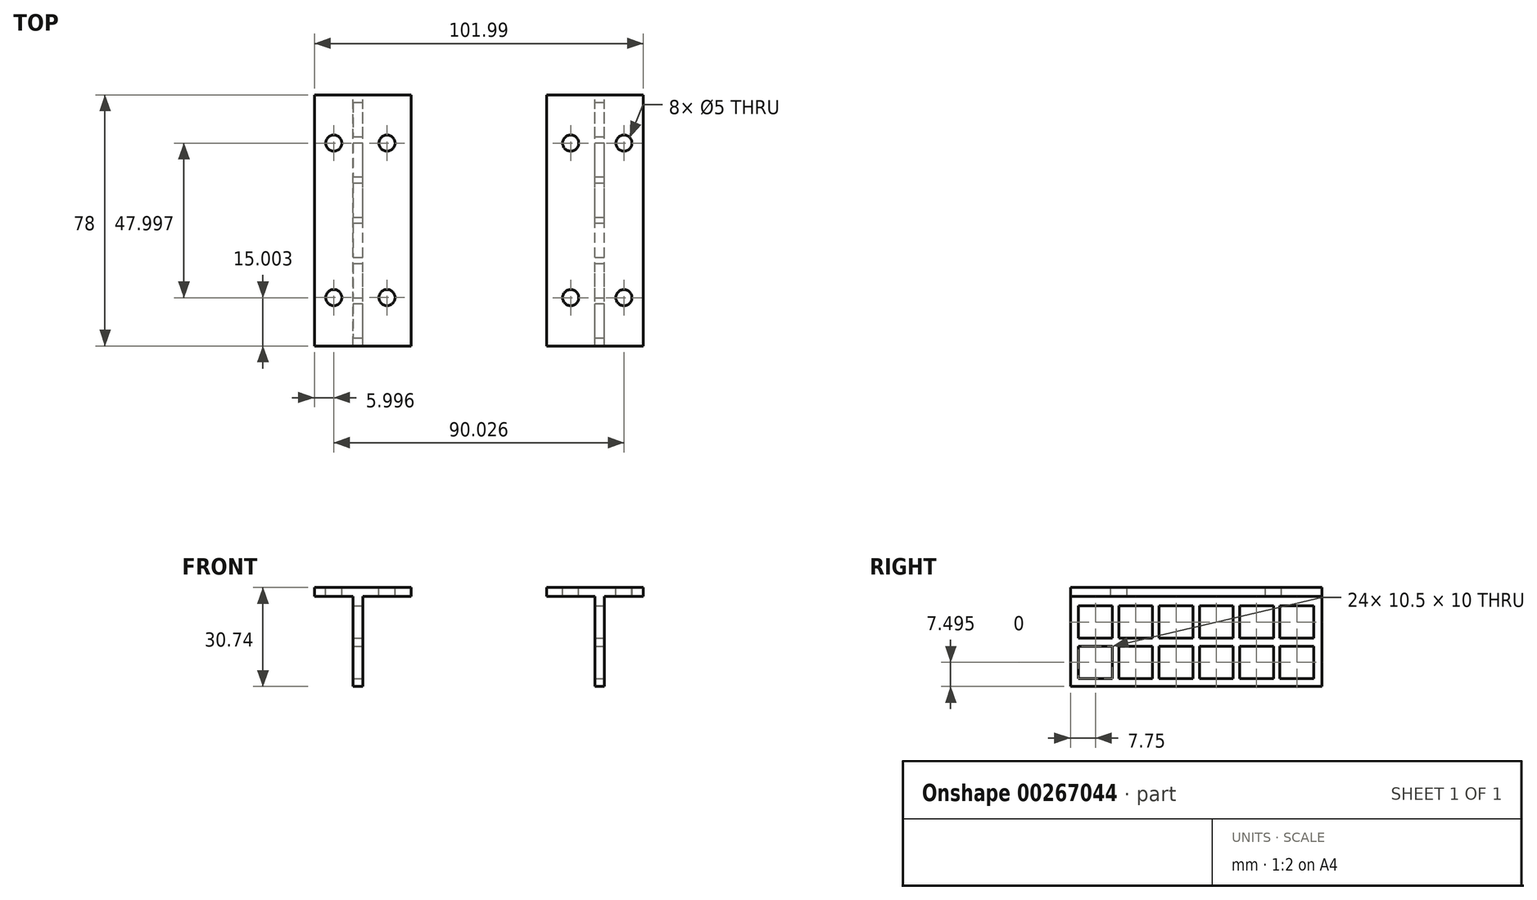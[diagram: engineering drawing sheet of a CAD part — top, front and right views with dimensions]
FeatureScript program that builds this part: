
annotation { "Feature Type Name" : "Feature", "Feature Type Description" : "" }
export const myFeature = defineFeature(function(context is Context, id is Id, definition is map)
    precondition{}
    {
        {
            var Q0;
            Q0=qCreatedBy(makeId("Front.planeOp"),FACE);
            var sketch = newSketch(context, id + "F0", { "sketchPlane" : qUnion([Q0])});
            skLineSegment(sketch, "E0", {"start": v(36.03, -9.62) * mm, "end": v(36.03, 18.38) * mm});
            skLineSegment(sketch, "E1", {"start": v(36.03, 18.38) * mm, "end": v(48.02, 18.38) * mm});
            skLineSegment(sketch, "E2", {"start": v(48.02, 18.38) * mm, "end": v(48.02, 21.12) * mm});
            skLineSegment(sketch, "E3", {"start": v(48.02, 21.12) * mm, "end": v(33.02, 21.12) * mm});
            skLineSegment(sketch, "E4", {"start": v(33.02, 18.38) * mm, "end": v(33.02, -9.62) * mm});
            skLineSegment(sketch, "E5.MirrorCS", {"start": v(-53.97, 18.38) * mm, "end": v(-53.97, 21.12) * mm});
            skLineSegment(sketch, "E6.MirrorCS", {"start": v(-41.97, -9.62) * mm, "end": v(-41.97, 18.38) * mm});
            skLineSegment(sketch, "E7.MirrorCS", {"start": v(-41.97, 18.38) * mm, "end": v(-53.97, 18.38) * mm});
            skLineSegment(sketch, "E8.MirrorCS", {"start": v(-53.97, 21.12) * mm, "end": v(-38.97, 21.12) * mm});
            skLineSegment(sketch, "E9.MirrorCS", {"start": v(-38.97, 18.38) * mm, "end": v(-38.97, -9.62) * mm});
            skPoint(sketch, "E10.MirrorCS.start.orphan", {"position": v(36.03, 18.38) * mm});
            skLineSegment(sketch, "E11", {"start": v(-41.97, -9.62) * mm, "end": v(-38.97, -9.62) * mm});
            skLineSegment(sketch, "E12", {"start": v(36.03, -9.62) * mm, "end": v(33.02, -9.62) * mm});
            skLineSegment(sketch, "E13.MirrorCS", {"start": v(-38.97, 18.38) * mm, "end": v(-23.97, 18.38) * mm});
            skLineSegment(sketch, "E14.MirrorCS", {"start": v(-23.97, 18.38) * mm, "end": v(-23.97, 21.12) * mm});
            skLineSegment(sketch, "E15.MirrorCS", {"start": v(-23.97, 21.12) * mm, "end": v(-38.97, 21.12) * mm});
            skPoint(sketch, "E16.orphan", {"position": v(-35.97, 18.38) * mm});
            skLineSegment(sketch, "E17.MirrorCS", {"start": v(33.02, 18.38) * mm, "end": v(18.02, 18.38) * mm});
            skLineSegment(sketch, "E18.MirrorCS", {"start": v(18.02, 18.38) * mm, "end": v(18.02, 21.12) * mm});
            skLineSegment(sketch, "E19.MirrorCS", {"start": v(18.02, 21.12) * mm, "end": v(33.02, 21.12) * mm});
            skPoint(sketch, "E20.orphan", {"position": v(30.02, 18.38) * mm});
            skSolve(sketch);
        }
        {
            var Q0;
            Q0=qSketchRegion(id+"F0",true);
            extrude(context, id + "F1", {"entities" : qUnion([Q0]), "endBound" : BoundingType.SYMMETRIC, "depth" : 78 * mm});
        }
        {
            var Q0;
            Q0=makeQuery(id+"F1.opExtrude","SWEPT_FACE",FACE,{"disambiguationData":[OSD([sQuery(id+"F0.wireOp",EDGE,"E3")])]});
            var sketch = newSketch(context, id + "F2", { "sketchPlane" : qUnion([Q0])});
            skLineSegment(sketch, "E21", {"start": v(42.02, -39) * mm, "end": v(42.06, 39) * mm, "construction": true});
            skLineSegment(sketch, "E22.0.0", {"start": v(-53.97, 39) * mm, "end": v(-53.97, 39) * mm});
            skLineSegment(sketch, "E22.0.1", {"start": v(-53.97, 39) * mm, "end": v(-53.97, -39) * mm, "construction": true});
            skLineSegment(sketch, "E22.0.2", {"start": v(-53.97, -39) * mm, "end": v(-53.97, -39) * mm});
            skLineSegment(sketch, "E22.0.3", {"start": v(-53.97, -39) * mm, "end": v(-53.97, 39) * mm, "construction": true});
            skLineSegment(sketch, "E23", {"start": v(-47.97, 39) * mm, "end": v(-47.97, -39) * mm, "construction": true});
            skLineSegment(sketch, "E24", {"start": v(-53.97, -23.96) * mm, "end": v(48.02, -24) * mm, "construction": true});
            skLineSegment(sketch, "E25", {"start": v(48.02, 24) * mm, "end": v(-53.97, 24) * mm, "construction": true});
            skLineSegment(sketch, "E26", {"start": v(48.02, -24) * mm, "end": v(48.02, -39) * mm, "construction": true});
            skLineSegment(sketch, "E27", {"start": v(48.02, 39) * mm, "end": v(48.02, 24) * mm, "construction": true});
            skCircle(sketch, "E28", {"center": v(42.03, -24) * mm, "radius": 2.5 * mm});
            skCircle(sketch, "E29", {"center": v(42.05, 24) * mm, "radius": 2.5 * mm});
            skCircle(sketch, "E30", {"center": v(-47.97, 24) * mm, "radius": 2.5 * mm});
            skCircle(sketch, "E31", {"center": v(-47.97, -23.96) * mm, "radius": 2.5 * mm});
            skCircle(sketch, "E32", {"center": v(25.52, -24) * mm, "radius": 2.5 * mm});
            skCircle(sketch, "E33", {"center": v(25.52, 24) * mm, "radius": 2.5 * mm});
            skCircle(sketch, "E34", {"center": v(-31.47, -23.97) * mm, "radius": 2.5 * mm});
            skCircle(sketch, "E35", {"center": v(-31.47, 24) * mm, "radius": 2.5 * mm});
            skLineSegment(sketch, "E36.0", {"start": v(-38.97, -39) * mm, "end": v(-38.97, 39) * mm, "construction": true});
            skLineSegment(sketch, "E37.0", {"start": v(33.02, -39) * mm, "end": v(33.02, 39) * mm, "construction": true});
            skLineSegment(sketch, "E38.0", {"start": v(-23.97, -39) * mm, "end": v(-23.97, 39) * mm, "construction": true});
            skLineSegment(sketch, "E39.0", {"start": v(18.02, -39) * mm, "end": v(18.02, 39) * mm, "construction": true});
            skLineSegment(sketch, "E40", {"start": v(-38.97, -31.27) * mm, "end": v(-23.97, -31.27) * mm, "construction": true});
            skLineSegment(sketch, "E41", {"start": v(33.02, -32.9) * mm, "end": v(18.02, -32.9) * mm, "construction": true});
            skPoint(sketch, "E42", {"position": v(-31.47, -31.27) * mm});
            skPoint(sketch, "E43", {"position": v(25.52, -32.9) * mm});
            skSolve(sketch);
        }
        {
            var Q0;
            Q0=qSketchRegion(id+"F2",true);
            extrude(context, id + "F3", {"entities" : qUnion([Q0]), "operationType" : NewBodyOperationType.REMOVE, "endBound" : BoundingType.UP_TO_NEXT, "oppositeDirection" : true, "depth" : 25 * mm});
        }
        {
            var Q0;
            Q0=makeQuery(id+"F1.opExtrude","SWEPT_FACE",FACE,{"disambiguationData":[OSD([sQuery(id+"F0.wireOp",EDGE,"E0")])]});
            var sketch = newSketch(context, id + "F4", { "sketchPlane" : qUnion([Q0])});
            skLineSegment(sketch, "E44.bottom", {"start": v(-36.5, -7.12) * mm, "end": v(-26.5, -7.12) * mm});
            skLineSegment(sketch, "E44.top", {"start": v(-36.5, 2.88) * mm, "end": v(-26.5, 2.88) * mm});
            skLineSegment(sketch, "E44.left", {"start": v(-36.5, -7.12) * mm, "end": v(-36.5, 2.88) * mm});
            skLineSegment(sketch, "E44.right", {"start": v(-26.5, -7.12) * mm, "end": v(-26.5, 2.88) * mm});
            skLineSegment(sketch, "E45.0.1.0", {"start": v(-36.5, 5.38) * mm, "end": v(-36.5, 15.38) * mm});
            skLineSegment(sketch, "E45.0.1.1", {"start": v(-26.5, 5.38) * mm, "end": v(-26.5, 15.38) * mm});
            skLineSegment(sketch, "E45.0.1.2", {"start": v(-36.5, 5.38) * mm, "end": v(-26.5, 5.38) * mm});
            skLineSegment(sketch, "E45.0.1.3", {"start": v(-36.5, 15.38) * mm, "end": v(-26.5, 15.38) * mm});
            skLineSegment(sketch, "E45.1.0.0", {"start": v(-24, -7.12) * mm, "end": v(-24, 2.88) * mm});
            skLineSegment(sketch, "E45.1.0.1", {"start": v(-14, -7.12) * mm, "end": v(-14, 2.88) * mm});
            skLineSegment(sketch, "E45.1.0.2", {"start": v(-24, -7.12) * mm, "end": v(-14, -7.12) * mm});
            skLineSegment(sketch, "E45.1.0.3", {"start": v(-24, 2.88) * mm, "end": v(-14, 2.88) * mm});
            skLineSegment(sketch, "E45.1.1.0", {"start": v(-24, 5.38) * mm, "end": v(-24, 15.38) * mm});
            skLineSegment(sketch, "E45.1.1.1", {"start": v(-14, 5.38) * mm, "end": v(-14, 15.38) * mm});
            skLineSegment(sketch, "E45.1.1.2", {"start": v(-24, 5.38) * mm, "end": v(-14, 5.38) * mm});
            skLineSegment(sketch, "E45.1.1.3", {"start": v(-24, 15.38) * mm, "end": v(-14, 15.38) * mm});
            skLineSegment(sketch, "E45.2.0.0", {"start": v(-11.5, -7.12) * mm, "end": v(-11.5, 2.88) * mm});
            skLineSegment(sketch, "E45.2.0.1", {"start": v(-1.5, -7.12) * mm, "end": v(-1.5, 2.88) * mm});
            skLineSegment(sketch, "E45.2.0.2", {"start": v(-11.5, -7.12) * mm, "end": v(-1.5, -7.12) * mm});
            skLineSegment(sketch, "E45.2.0.3", {"start": v(-11.5, 2.88) * mm, "end": v(-1.5, 2.88) * mm});
            skLineSegment(sketch, "E45.2.1.0", {"start": v(-11.5, 5.38) * mm, "end": v(-11.5, 15.38) * mm});
            skLineSegment(sketch, "E45.2.1.1", {"start": v(-1.5, 5.38) * mm, "end": v(-1.5, 15.38) * mm});
            skLineSegment(sketch, "E45.2.1.2", {"start": v(-11.5, 5.38) * mm, "end": v(-1.5, 5.38) * mm});
            skLineSegment(sketch, "E45.2.1.3", {"start": v(-11.5, 15.38) * mm, "end": v(-1.5, 15.38) * mm});
            skLineSegment(sketch, "E45.3.0.0", {"start": v(1, -7.12) * mm, "end": v(1, 2.88) * mm});
            skLineSegment(sketch, "E45.3.0.1", {"start": v(11, -7.12) * mm, "end": v(11, 2.88) * mm});
            skLineSegment(sketch, "E45.3.0.2", {"start": v(1, -7.12) * mm, "end": v(11, -7.12) * mm});
            skLineSegment(sketch, "E45.3.0.3", {"start": v(1, 2.88) * mm, "end": v(11, 2.88) * mm});
            skLineSegment(sketch, "E45.3.1.0", {"start": v(1, 5.38) * mm, "end": v(1, 15.38) * mm});
            skLineSegment(sketch, "E45.3.1.1", {"start": v(11, 5.38) * mm, "end": v(11, 15.38) * mm});
            skLineSegment(sketch, "E45.3.1.2", {"start": v(1, 5.38) * mm, "end": v(11, 5.38) * mm});
            skLineSegment(sketch, "E45.3.1.3", {"start": v(1, 15.38) * mm, "end": v(11, 15.38) * mm});
            skLineSegment(sketch, "E45.4.0.0", {"start": v(13.5, -7.12) * mm, "end": v(13.5, 2.88) * mm});
            skLineSegment(sketch, "E45.4.0.1", {"start": v(23.5, -7.12) * mm, "end": v(23.5, 2.88) * mm});
            skLineSegment(sketch, "E45.4.0.2", {"start": v(13.5, -7.12) * mm, "end": v(23.5, -7.12) * mm});
            skLineSegment(sketch, "E45.4.0.3", {"start": v(13.5, 2.88) * mm, "end": v(23.5, 2.88) * mm});
            skLineSegment(sketch, "E45.4.1.0", {"start": v(13.5, 5.38) * mm, "end": v(13.5, 15.38) * mm});
            skLineSegment(sketch, "E45.4.1.1", {"start": v(23.5, 5.38) * mm, "end": v(23.5, 15.38) * mm});
            skLineSegment(sketch, "E45.4.1.2", {"start": v(13.5, 5.38) * mm, "end": v(23.5, 5.38) * mm});
            skLineSegment(sketch, "E45.4.1.3", {"start": v(13.5, 15.38) * mm, "end": v(23.5, 15.38) * mm});
            skLineSegment(sketch, "E45.5.0.0", {"start": v(26, -7.12) * mm, "end": v(26, 2.88) * mm});
            skLineSegment(sketch, "E45.5.0.1", {"start": v(36, -7.12) * mm, "end": v(36, 2.88) * mm});
            skLineSegment(sketch, "E45.5.0.2", {"start": v(26, -7.12) * mm, "end": v(36, -7.12) * mm});
            skLineSegment(sketch, "E45.5.0.3", {"start": v(26, 2.88) * mm, "end": v(36, 2.88) * mm});
            skLineSegment(sketch, "E45.5.1.0", {"start": v(26, 5.38) * mm, "end": v(26, 15.38) * mm});
            skLineSegment(sketch, "E45.5.1.1", {"start": v(36, 5.38) * mm, "end": v(36, 15.38) * mm});
            skLineSegment(sketch, "E45.5.1.2", {"start": v(26, 5.38) * mm, "end": v(36, 5.38) * mm});
            skLineSegment(sketch, "E45.5.1.3", {"start": v(26, 15.38) * mm, "end": v(36, 15.38) * mm});
            skLineSegment(sketch, "E45.direction1", {"start": v(-36.5, -7.12) * mm, "end": v(-24, -7.12) * mm, "construction": true});
            skLineSegment(sketch, "E45.direction2", {"start": v(-36.5, -7.12) * mm, "end": v(-36.5, 5.38) * mm, "construction": true});
            skSolve(sketch);
        }
        {
            var Q0;
            Q0=qSketchRegion(id+"F4",true);
            var Q1;
            Q1=makeQuery(id+"F1.opExtrude","SWEPT_FACE",FACE,{"disambiguationData":[OSD([sQuery(id+"F0.wireOp",EDGE,"E6.MirrorCS")])]});
            extrude(context, id + "F5", {"entities" : qUnion([Q0]), "operationType" : NewBodyOperationType.REMOVE, "endBound" : BoundingType.THROUGH_ALL, "oppositeDirection" : true, "endBoundEntityFace" : qUnion([Q1]), "depth" : 86.9 * mm});
        }
        {
            var Q0;
            Q0=makeQuery(id+"F1.opExtrude","SWEPT_FACE",FACE,{"disambiguationData":[OSD([sQuery(id+"F0.wireOp",EDGE,"E6.MirrorCS")])]});
            var sketch = newSketch(context, id + "F6", { "sketchPlane" : qUnion([Q0])});
            skLineSegment(sketch, "E46.bottom", {"start": v(-36.5, -7.12) * mm, "end": v(-26.5, -7.12) * mm});
            skLineSegment(sketch, "E46.top", {"start": v(-36.5, 2.88) * mm, "end": v(-26.5, 2.88) * mm});
            skLineSegment(sketch, "E46.left", {"start": v(-36.5, -7.12) * mm, "end": v(-36.5, 2.88) * mm});
            skLineSegment(sketch, "E46.right", {"start": v(-26.5, -7.12) * mm, "end": v(-26.5, 2.88) * mm});
            skLineSegment(sketch, "E47.0.1.0", {"start": v(-36.5, 5.38) * mm, "end": v(-26.5, 5.38) * mm});
            skLineSegment(sketch, "E47.0.1.1", {"start": v(-36.5, 15.38) * mm, "end": v(-26.5, 15.38) * mm});
            skLineSegment(sketch, "E47.0.1.2", {"start": v(-36.5, 5.38) * mm, "end": v(-36.5, 15.38) * mm});
            skLineSegment(sketch, "E47.0.1.3", {"start": v(-26.5, 5.38) * mm, "end": v(-26.5, 15.38) * mm});
            skLineSegment(sketch, "E47.1.0.0", {"start": v(-24, -7.12) * mm, "end": v(-14, -7.12) * mm});
            skLineSegment(sketch, "E47.1.0.1", {"start": v(-24, 2.88) * mm, "end": v(-14, 2.88) * mm});
            skLineSegment(sketch, "E47.1.0.2", {"start": v(-24, -7.12) * mm, "end": v(-24, 2.88) * mm});
            skLineSegment(sketch, "E47.1.0.3", {"start": v(-14, -7.12) * mm, "end": v(-14, 2.88) * mm});
            skLineSegment(sketch, "E47.1.1.0", {"start": v(-24, 5.38) * mm, "end": v(-14, 5.38) * mm});
            skLineSegment(sketch, "E47.1.1.1", {"start": v(-24, 15.38) * mm, "end": v(-14, 15.38) * mm});
            skLineSegment(sketch, "E47.1.1.2", {"start": v(-24, 5.38) * mm, "end": v(-24, 15.38) * mm});
            skLineSegment(sketch, "E47.1.1.3", {"start": v(-14, 5.38) * mm, "end": v(-14, 15.38) * mm});
            skLineSegment(sketch, "E47.2.0.0", {"start": v(-11.5, -7.12) * mm, "end": v(-1.5, -7.12) * mm});
            skLineSegment(sketch, "E47.2.0.1", {"start": v(-11.5, 2.88) * mm, "end": v(-1.5, 2.88) * mm});
            skLineSegment(sketch, "E47.2.0.2", {"start": v(-11.5, -7.12) * mm, "end": v(-11.5, 2.88) * mm});
            skLineSegment(sketch, "E47.2.0.3", {"start": v(-1.5, -7.12) * mm, "end": v(-1.5, 2.88) * mm});
            skLineSegment(sketch, "E47.2.1.0", {"start": v(-11.5, 5.38) * mm, "end": v(-1.5, 5.38) * mm});
            skLineSegment(sketch, "E47.2.1.1", {"start": v(-11.5, 15.38) * mm, "end": v(-1.5, 15.38) * mm});
            skLineSegment(sketch, "E47.2.1.2", {"start": v(-11.5, 5.38) * mm, "end": v(-11.5, 15.38) * mm});
            skLineSegment(sketch, "E47.2.1.3", {"start": v(-1.5, 5.38) * mm, "end": v(-1.5, 15.38) * mm});
            skLineSegment(sketch, "E47.3.0.0", {"start": v(1, -7.12) * mm, "end": v(11, -7.12) * mm});
            skLineSegment(sketch, "E47.3.0.1", {"start": v(1, 2.88) * mm, "end": v(11, 2.88) * mm});
            skLineSegment(sketch, "E47.3.0.2", {"start": v(1, -7.12) * mm, "end": v(1, 2.88) * mm});
            skLineSegment(sketch, "E47.3.0.3", {"start": v(11, -7.12) * mm, "end": v(11, 2.88) * mm});
            skLineSegment(sketch, "E47.3.1.0", {"start": v(1, 5.38) * mm, "end": v(11, 5.38) * mm});
            skLineSegment(sketch, "E47.3.1.1", {"start": v(1, 15.38) * mm, "end": v(11, 15.38) * mm});
            skLineSegment(sketch, "E47.3.1.2", {"start": v(1, 5.38) * mm, "end": v(1, 15.38) * mm});
            skLineSegment(sketch, "E47.3.1.3", {"start": v(11, 5.38) * mm, "end": v(11, 15.38) * mm});
            skLineSegment(sketch, "E47.4.0.0", {"start": v(13.5, -7.12) * mm, "end": v(23.5, -7.12) * mm});
            skLineSegment(sketch, "E47.4.0.1", {"start": v(13.5, 2.88) * mm, "end": v(23.5, 2.88) * mm});
            skLineSegment(sketch, "E47.4.0.2", {"start": v(13.5, -7.12) * mm, "end": v(13.5, 2.88) * mm});
            skLineSegment(sketch, "E47.4.0.3", {"start": v(23.5, -7.12) * mm, "end": v(23.5, 2.88) * mm});
            skLineSegment(sketch, "E47.4.1.0", {"start": v(13.5, 5.38) * mm, "end": v(23.5, 5.38) * mm});
            skLineSegment(sketch, "E47.4.1.1", {"start": v(13.5, 15.38) * mm, "end": v(23.5, 15.38) * mm});
            skLineSegment(sketch, "E47.4.1.2", {"start": v(13.5, 5.38) * mm, "end": v(13.5, 15.38) * mm});
            skLineSegment(sketch, "E47.4.1.3", {"start": v(23.5, 5.38) * mm, "end": v(23.5, 15.38) * mm});
            skLineSegment(sketch, "E47.5.0.0", {"start": v(26, -7.12) * mm, "end": v(36, -7.12) * mm});
            skLineSegment(sketch, "E47.5.0.1", {"start": v(26, 2.88) * mm, "end": v(36, 2.88) * mm});
            skLineSegment(sketch, "E47.5.0.2", {"start": v(26, -7.12) * mm, "end": v(26, 2.88) * mm});
            skLineSegment(sketch, "E47.5.0.3", {"start": v(36, -7.12) * mm, "end": v(36, 2.88) * mm});
            skLineSegment(sketch, "E47.5.1.0", {"start": v(26, 5.38) * mm, "end": v(36, 5.38) * mm});
            skLineSegment(sketch, "E47.5.1.1", {"start": v(26, 15.38) * mm, "end": v(36, 15.38) * mm});
            skLineSegment(sketch, "E47.5.1.2", {"start": v(26, 5.38) * mm, "end": v(26, 15.38) * mm});
            skLineSegment(sketch, "E47.5.1.3", {"start": v(36, 5.38) * mm, "end": v(36, 15.38) * mm});
            skLineSegment(sketch, "E47.direction1", {"start": v(-36.5, -7.12) * mm, "end": v(-24, -7.12) * mm, "construction": true});
            skLineSegment(sketch, "E47.direction2", {"start": v(-36.5, -7.12) * mm, "end": v(-36.5, 5.38) * mm, "construction": true});
            skSolve(sketch);
        }
        {
            var Q0;
            Q0=qSketchRegion(id+"F6",true);
            extrude(context, id + "F7", {"entities" : qUnion([Q0]), "operationType" : NewBodyOperationType.REMOVE, "endBound" : BoundingType.THROUGH_ALL, "oppositeDirection" : true, "depth" : 25 * mm});
        }
    });
